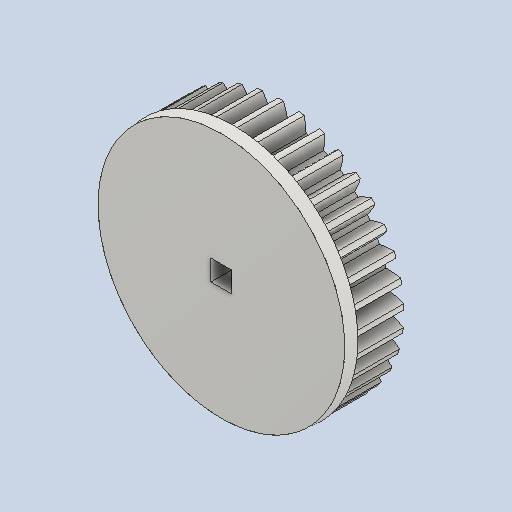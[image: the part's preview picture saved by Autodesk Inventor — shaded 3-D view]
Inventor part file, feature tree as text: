
AUTODESK INVENTOR PART (.ipt)
format: ipt  version: 2022 (Build 260153000, 153)  size: 703,488 bytes
history: native  units: in
note: dims shown in document units (in); Inventor stores cm internally (conversion verified against a paired STEP export)
features: other x12, sketch x5, plane x3
ambient origin geometry x8: Origin, YZ Plane, XZ Plane, XY Plane, X Axis, Y Axis, Z Axis, Center Point
bodies: Solid1 (feature_tree)
feature tree (20):
  other  "Spur Gear21_MIR.ipt"
  other  "Solid1::Spur Gear21_MIR.ipt"
  other  "TaggingFeature1"
  sketch  "Sketch1"  dims[d0=0.3937in]
  sketch  "Sketch2"  dims[d9=0.0in d14=0.0in d15=0.9352in d16=0.0in d17=0.0in d18=0.0in d19=0.9352in]
  sketch  "Sketch3"
  sketch  "Sketch4"
  sketch  "Sketch5"
  plane  "XZ Plane_1"
  plane  "Work Plane2"
  plane  "Work Plane3"
  other  "Srf1"
  other  "Srf1::Derived"
  other  "Start plane iMate"
  other  "Distance iMate"
  other  "Position iMate"
  other  "Mesh iMate"
  other  "Axis iMate"
  other  "Mesh iMate2"
  other  "Align iMate"
